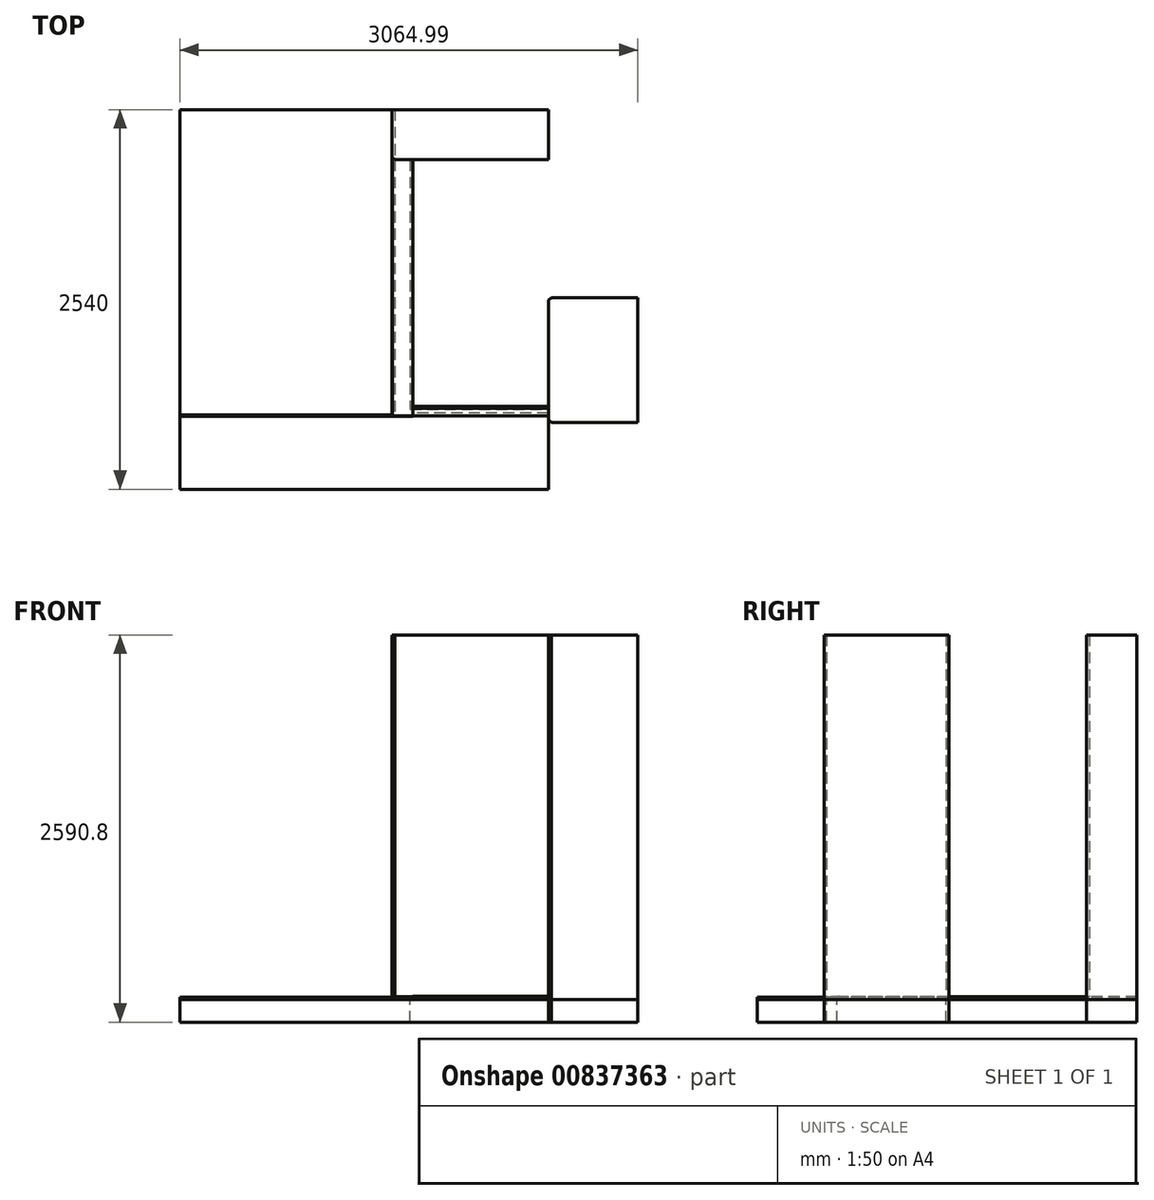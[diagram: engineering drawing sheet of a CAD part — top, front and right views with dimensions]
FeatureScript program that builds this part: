
annotation { "Feature Type Name" : "Feature", "Feature Type Description" : "" }
export const myFeature = defineFeature(function(context is Context, id is Id, definition is map)
    precondition{}
    {
        {
            var Q0;
            Q0=qCreatedBy(makeId("Top.planeOp"),FACE);
            var sketch = newSketch(context, id + "F0", { "sketchPlane" : qUnion([Q0])});
            skLineSegment(sketch, "E0.bottom", {"start": v(702.07, 1267.57) * mm, "end": v(-838.87, 1267.57) * mm});
            skLineSegment(sketch, "E0.top", {"start": v(702.07, -1272.43) * mm, "end": v(-838.87, -1272.43) * mm});
            skLineSegment(sketch, "E0.left", {"start": v(702.07, 1267.57) * mm, "end": v(702.07, -1272.43) * mm});
            skLineSegment(sketch, "E0.right", {"start": v(-838.87, 1267.57) * mm, "end": v(-838.87, -1272.43) * mm});
            skLineSegment(sketch, "E1.bottom", {"start": v(702.07, -1272.43) * mm, "end": v(1629.17, -1272.43) * mm});
            skLineSegment(sketch, "E1.top", {"start": v(702.07, -738.85) * mm, "end": v(1629.17, -738.85) * mm});
            skLineSegment(sketch, "E1.left", {"start": v(702.07, -1272.43) * mm, "end": v(702.07, -738.85) * mm});
            skLineSegment(sketch, "E1.right", {"start": v(1629.17, -1272.43) * mm, "end": v(1629.17, -738.85) * mm});
            skLineSegment(sketch, "E2.bottom", {"start": v(702.07, 1267.57) * mm, "end": v(1629.17, 1267.57) * mm});
            skLineSegment(sketch, "E2.top", {"start": v(702.07, 931.2) * mm, "end": v(1629.17, 931.2) * mm});
            skLineSegment(sketch, "E2.left", {"start": v(702.07, 1267.57) * mm, "end": v(702.07, 931.2) * mm});
            skLineSegment(sketch, "E2.right", {"start": v(1629.17, 1267.57) * mm, "end": v(1629.17, 931.2) * mm});
            skSolve(sketch);
        }
        {
            var Q0;
            Q0=makeQuery(id+"F0.imprint","IMPRINT",FACE,{"disambiguationData":[TD([[makeQuery(id+"F0.imprint","IMPRINT",EDGE,{"derivedFrom":sQuery(id+"F0.wireOp",EDGE,"E0.bottom")}),1.0]])]});
            var Q1;
            Q1=makeQuery(id+"F0.imprint","IMPRINT",FACE,{"disambiguationData":[TD([[makeQuery(id+"F0.imprint","IMPRINT",EDGE,{"derivedFrom":sQuery(id+"F0.wireOp",EDGE,"E2.bottom")}),-1.0]])]});
            var Q2;
            Q2=makeQuery(id+"F0.imprint","IMPRINT",FACE,{"disambiguationData":[TD([[makeQuery(id+"F0.imprint","IMPRINT",EDGE,{"derivedFrom":sQuery(id+"F0.wireOp",EDGE,"E1.bottom")}),1.0]])]});
            extrude(context, id + "F1", {"entities" : qUnion([Q0, Q1, Q2]), "oppositeDirection" : true, "depth" : 152.4 * mm, "offsetDistance" : 25.4 * mm});
        }
        {
            var Q0;
            Q0=makeQuery(id+"F1.opExtrude","CAP_FACE",FACE,{"disambiguationData":[OSD([sQuery(id+"F0.wireOp",EDGE,"E0.bottom"),sQuery(id+"F0.wireOp",EDGE,"E0.top"),sQuery(id+"F0.wireOp",EDGE,"E0.left"),sQuery(id+"F0.wireOp",EDGE,"E0.right"),sQuery(id+"F0.wireOp",EDGE,"E1.bottom"),sQuery(id+"F0.wireOp",EDGE,"E1.top"),sQuery(id+"F0.wireOp",EDGE,"E1.right"),sQuery(id+"F0.wireOp",EDGE,"E2.bottom"),sQuery(id+"F0.wireOp",EDGE,"E2.top"),sQuery(id+"F0.wireOp",EDGE,"E2.right")])],"isStart":true});
            var sketch = newSketch(context, id + "F2", { "sketchPlane" : qUnion([Q0])});
            skLineSegment(sketch, "E3", {"start": v(702.07, 931.2) * mm, "end": v(600.47, 931.2) * mm});
            skLineSegment(sketch, "E4", {"start": v(600.47, 931.2) * mm, "end": v(582.5, 949.16) * mm});
            skLineSegment(sketch, "E5", {"start": v(582.5, 949.16) * mm, "end": v(582.5, 1267.57) * mm});
            skLineSegment(sketch, "E6", {"start": v(582.5, 1267.57) * mm, "end": v(1629.17, 1267.57) * mm});
            skLineSegment(sketch, "E7", {"start": v(1629.17, 1267.57) * mm, "end": v(1629.17, 931.2) * mm});
            skLineSegment(sketch, "E8", {"start": v(1629.17, 931.2) * mm, "end": v(702.07, 931.2) * mm});
            skSolve(sketch);
        }
        {
            var Q0;
            Q0=makeQuery(id+"F2.imprint","IMPRINT",FACE,{"disambiguationData":[TD([[makeQuery(id+"F2.imprint","IMPRINT",EDGE,{"derivedFrom":sQuery(id+"F2.wireOp",EDGE,"E3")}),-1.0]])]});
            extrude(context, id + "F3", {"entities" : qUnion([Q0]), "depth" : 2438.4 * mm, "offsetDistance" : 25.4 * mm});
        }
        {
            var Q0;
            Q0=makeQuery(id+"F1.opExtrude","CAP_FACE",FACE,{"disambiguationData":[OSD([sQuery(id+"F0.wireOp",EDGE,"E0.bottom"),sQuery(id+"F0.wireOp",EDGE,"E0.top"),sQuery(id+"F0.wireOp",EDGE,"E0.left"),sQuery(id+"F0.wireOp",EDGE,"E0.right"),sQuery(id+"F0.wireOp",EDGE,"E1.bottom"),sQuery(id+"F0.wireOp",EDGE,"E1.top"),sQuery(id+"F0.wireOp",EDGE,"E1.right"),sQuery(id+"F0.wireOp",EDGE,"E2.bottom"),sQuery(id+"F0.wireOp",EDGE,"E2.top"),sQuery(id+"F0.wireOp",EDGE,"E2.right")])],"isStart":true});
            var sketch = newSketch(context, id + "F4", { "sketchPlane" : qUnion([Q0])});
            skLineSegment(sketch, "E9", {"start": v(1629.17, -808.7) * mm, "end": v(1629.17, -738.85) * mm});
            skLineSegment(sketch, "E10", {"start": v(1629.17, -738.85) * mm, "end": v(1629.17, -8.6) * mm});
            skLineSegment(sketch, "E11", {"start": v(1629.17, -8.6) * mm, "end": v(1647.13, 9.36) * mm});
            skLineSegment(sketch, "E12", {"start": v(1647.13, 9.36) * mm, "end": v(2226.12, 9.36) * mm});
            skLineSegment(sketch, "E13", {"start": v(1629.17, -808.7) * mm, "end": v(1647.13, -826.66) * mm});
            skLineSegment(sketch, "E14", {"start": v(1647.13, -826.66) * mm, "end": v(2226.12, -826.66) * mm});
            skLineSegment(sketch, "E15", {"start": v(2226.12, -826.66) * mm, "end": v(2226.12, 9.36) * mm});
            skSolve(sketch);
        }
        {
            var Q0;
            Q0=makeQuery(id+"F4.imprint","IMPRINT",FACE,{"disambiguationData":[TD([[makeQuery(id+"F4.imprint","IMPRINT",EDGE,{"derivedFrom":sQuery(id+"F4.wireOp",EDGE,"E9")}),-1.0]])]});
            var Q1;
            Q1=makeQuery(id+"F1.opExtrude","CAP_FACE",FACE,{"disambiguationData":[OSD([sQuery(id+"F0.wireOp",EDGE,"E0.bottom"),sQuery(id+"F0.wireOp",EDGE,"E0.top"),sQuery(id+"F0.wireOp",EDGE,"E0.left"),sQuery(id+"F0.wireOp",EDGE,"E0.right"),sQuery(id+"F0.wireOp",EDGE,"E1.bottom"),sQuery(id+"F0.wireOp",EDGE,"E1.top"),sQuery(id+"F0.wireOp",EDGE,"E1.right"),sQuery(id+"F0.wireOp",EDGE,"E2.bottom"),sQuery(id+"F0.wireOp",EDGE,"E2.top"),sQuery(id+"F0.wireOp",EDGE,"E2.right")])],"isStart":false});
            extrude(context, id + "F5", {"entities" : qUnion([Q0]), "operationType" : NewBodyOperationType.ADD, "endBound" : BoundingType.UP_TO_SURFACE, "oppositeDirection" : true, "depth" : 25.4 * mm, "endBoundEntityFace" : qUnion([Q1]), "offsetDistance" : 25.4 * mm});
        }
        {
            var Q0;
            Q0=makeQuery(id+"F4.imprint","IMPRINT",FACE,{"disambiguationData":[TD([[makeQuery(id+"F4.imprint","IMPRINT",EDGE,{"derivedFrom":sQuery(id+"F4.wireOp",EDGE,"E9")}),-1.0]])]});
            var Q1;
            Q1=makeQuery(id+"F3.opExtrude","CAP_FACE",FACE,{"disambiguationData":[OSD([sQuery(id+"F2.wireOp",EDGE,"E3"),sQuery(id+"F2.wireOp",EDGE,"E4"),sQuery(id+"F2.wireOp",EDGE,"E5"),sQuery(id+"F2.wireOp",EDGE,"E6"),sQuery(id+"F2.wireOp",EDGE,"E7"),sQuery(id+"F2.wireOp",EDGE,"E8")])],"isStart":false});
            extrude(context, id + "F6", {"entities" : qUnion([Q0]), "endBound" : BoundingType.UP_TO_SURFACE, "depth" : 25.4 * mm, "endBoundEntityFace" : qUnion([Q1]), "offsetDistance" : 25.4 * mm});
        }
        {
            var Q0;
            Q0=makeQuery(id+"F5.boolean.opBoolean","MERGE",FACE,{"derivedFrom":[makeQuery(id+"F1.opExtrude","CAP_FACE",FACE,{"disambiguationData":[OSD([sQuery(id+"F0.wireOp",EDGE,"E0.bottom"),sQuery(id+"F0.wireOp",EDGE,"E0.top"),sQuery(id+"F0.wireOp",EDGE,"E0.left"),sQuery(id+"F0.wireOp",EDGE,"E0.right"),sQuery(id+"F0.wireOp",EDGE,"E1.bottom"),sQuery(id+"F0.wireOp",EDGE,"E1.top"),sQuery(id+"F0.wireOp",EDGE,"E1.right"),sQuery(id+"F0.wireOp",EDGE,"E2.bottom"),sQuery(id+"F0.wireOp",EDGE,"E2.top"),sQuery(id+"F0.wireOp",EDGE,"E2.right")])],"isStart":true}),makeQuery(id+"F5.opExtrude","CAP_FACE",FACE,{"disambiguationData":[OSD([sQuery(id+"F4.wireOp",EDGE,"E9"),sQuery(id+"F4.wireOp",EDGE,"E10"),sQuery(id+"F4.wireOp",EDGE,"E11"),sQuery(id+"F4.wireOp",EDGE,"E12"),sQuery(id+"F4.wireOp",EDGE,"E13"),sQuery(id+"F4.wireOp",EDGE,"E14"),sQuery(id+"F4.wireOp",EDGE,"E15")])],"isStart":true})]});
            var sketch = newSketch(context, id + "F7", { "sketchPlane" : qUnion([Q0])});
            skLineSegment(sketch, "E16", {"start": v(600.47, 931.2) * mm, "end": v(582.5, 949.16) * mm});
            skLineSegment(sketch, "E17", {"start": v(582.5, 949.16) * mm, "end": v(582.5, -785.23) * mm});
            skLineSegment(sketch, "E18", {"start": v(721.12, 931.2) * mm, "end": v(721.12, -785.23) * mm});
            skLineSegment(sketch, "E19", {"start": v(721.12, -785.23) * mm, "end": v(582.5, -785.23) * mm});
            skLineSegment(sketch, "E20", {"start": v(600.47, 931.2) * mm, "end": v(721.12, 931.2) * mm});
            skSolve(sketch);
        }
        {
            var Q0;
            {var subQ4=sQuery(id+"F7.wireOp",EDGE,"E16");Q0=makeQuery(id+"F7.imprint","IMPRINT",FACE,{"disambiguationData":[TD([[makeQuery(id+"F7.imprint","IMPRINT",EDGE,{"derivedFrom":subQ4}),1.0]])]});}
            var Q1;
            {var subQ5=makeQuery(id+"F1.opExtrude","CAP_EDGE",EDGE,{"disambiguationData":[OSD([sQuery(id+"F0.wireOp",EDGE,"E0.left")])],"isStart":true});Q1=makeQuery(id+"F7.imprint","IMPRINT",FACE,{"disambiguationData":[TD([[makeQuery(id+"F7.imprint","IMPRINT",EDGE,{"derivedFrom":subQ5}),1.0]])]});}
            extrude(context, id + "F8", {"entities" : qUnion([Q0, Q1]), "depth" : 19.05 * mm, "offsetDistance" : 25.4 * mm});
        }
        {
            var Q0;
            Q0=makeQuery(id+"F5.boolean.opBoolean","MERGE",FACE,{"derivedFrom":[makeQuery(id+"F1.opExtrude","CAP_FACE",FACE,{"disambiguationData":[OSD([sQuery(id+"F0.wireOp",EDGE,"E0.bottom"),sQuery(id+"F0.wireOp",EDGE,"E0.top"),sQuery(id+"F0.wireOp",EDGE,"E0.left"),sQuery(id+"F0.wireOp",EDGE,"E0.right"),sQuery(id+"F0.wireOp",EDGE,"E1.bottom"),sQuery(id+"F0.wireOp",EDGE,"E1.top"),sQuery(id+"F0.wireOp",EDGE,"E1.right"),sQuery(id+"F0.wireOp",EDGE,"E2.bottom"),sQuery(id+"F0.wireOp",EDGE,"E2.top"),sQuery(id+"F0.wireOp",EDGE,"E2.right")])],"isStart":true}),makeQuery(id+"F5.opExtrude","CAP_FACE",FACE,{"disambiguationData":[OSD([sQuery(id+"F4.wireOp",EDGE,"E9"),sQuery(id+"F4.wireOp",EDGE,"E10"),sQuery(id+"F4.wireOp",EDGE,"E11"),sQuery(id+"F4.wireOp",EDGE,"E12"),sQuery(id+"F4.wireOp",EDGE,"E13"),sQuery(id+"F4.wireOp",EDGE,"E14"),sQuery(id+"F4.wireOp",EDGE,"E15")])],"isStart":true})]});
            var sketch = newSketch(context, id + "F9", { "sketchPlane" : qUnion([Q0])});
            skLineSegment(sketch, "E21", {"start": v(582.5, 1267.57) * mm, "end": v(-838.87, 1267.57) * mm});
            skLineSegment(sketch, "E22", {"start": v(-838.87, 1267.57) * mm, "end": v(-838.87, -1272.43) * mm});
            skLineSegment(sketch, "E23", {"start": v(-838.87, -1272.43) * mm, "end": v(1629.17, -1272.43) * mm});
            skLineSegment(sketch, "E24", {"start": v(1629.17, -1272.43) * mm, "end": v(1629.17, -779.67) * mm});
            skLineSegment(sketch, "E25", {"start": v(1629.17, -779.67) * mm, "end": v(597.3, -779.67) * mm});
            skLineSegment(sketch, "E26", {"start": v(582.5, 1267.57) * mm, "end": v(582.5, 949.16) * mm});
            skLineSegment(sketch, "E27", {"start": v(582.5, 949.16) * mm, "end": v(597.3, 934.37) * mm});
            skLineSegment(sketch, "E28", {"start": v(597.3, 934.37) * mm, "end": v(597.3, -779.67) * mm});
            skSolve(sketch);
        }
        {
            var Q0;
            Q0=makeQuery(id+"F9.imprint","IMPRINT",FACE,{"disambiguationData":[TD([[makeQuery(id+"F9.imprint","IMPRINT",EDGE,{"derivedFrom":sQuery(id+"F9.wireOp",EDGE,"E21")}),1.0]])]});
            extrude(context, id + "F10", {"entities" : qUnion([Q0]), "depth" : 2.3 * mm, "offsetDistance" : 25.4 * mm});
        }
        {
            var Q0;
            Q0=makeQuery(id+"F10.opExtrude","CAP_FACE",FACE,{"disambiguationData":[OSD([sQuery(id+"F9.wireOp",EDGE,"E21"),sQuery(id+"F9.wireOp",EDGE,"E22"),sQuery(id+"F9.wireOp",EDGE,"E23"),sQuery(id+"F9.wireOp",EDGE,"E24"),sQuery(id+"F9.wireOp",EDGE,"E25"),sQuery(id+"F9.wireOp",EDGE,"E26"),sQuery(id+"F9.wireOp",EDGE,"E27"),sQuery(id+"F9.wireOp",EDGE,"E28")])],"isStart":false});
            extrude(context, id + "F11", {"entities" : qUnion([Q0]), "depth" : 11.43 * mm, "offsetDistance" : 25.4 * mm});
        }
        {
            var Q0;
            Q0=makeQuery(id+"F8.opExtrude","SWEPT_FACE",FACE,{"disambiguationData":[OSD([sQuery(id+"F7.wireOp",EDGE,"E18")])]});
            var sketch = newSketch(context, id + "F12", { "sketchPlane" : qUnion([Q0])});
            skLineSegment(sketch, "E29", {"start": v(-738.85, 0) * mm, "end": v(-762.98, 0) * mm});
            skLineSegment(sketch, "E30", {"start": v(-762.98, 0) * mm, "end": v(-762.98, 14.48) * mm});
            skLineSegment(sketch, "E31", {"start": v(-762.98, 14.48) * mm, "end": v(-778.22, 14.48) * mm});
            skLineSegment(sketch, "E32", {"start": v(-778.22, 19.56) * mm, "end": v(-729.7, 19.56) * mm});
            skLineSegment(sketch, "E33", {"start": v(-738.85, 0) * mm, "end": v(-738.85, -3.3) * mm});
            skLineSegment(sketch, "E34", {"start": v(-738.85, -3.3) * mm, "end": v(-729.7, -3.3) * mm});
            skArc(sketch, "E35", {"start": v(-729.7, -3.3) * mm, "mid": v(-717.9, 8.13) * mm, "end": v(-729.7, 19.56) * mm});
            skLineSegment(sketch, "E36", {"start": v(-717.9, 8.13) * mm, "end": v(-778.22, 8.13) * mm, "construction": true});
            skPoint(sketch, "E36.startSnap0", {"position": v(-717.9, 8.13) * mm});
            skArc(sketch, "E37", {"start": v(-778.22, 19.56) * mm, "mid": v(-780.76, 17.02) * mm, "end": v(-778.22, 14.48) * mm});
            skSolve(sketch);
        }
        {
            var Q0;
            {var subQ9=sQuery(id+"F12.wireOp",EDGE,"E29");Q0=makeQuery(id+"F12.imprint","IMPRINT",FACE,{"disambiguationData":[TD([[makeQuery(id+"F12.imprint","IMPRINT",EDGE,{"derivedFrom":subQ9}),-1.0]])]});}
            var Q1;
            {var subQ0=sQuery(id+"F12.wireOp",EDGE,"E32");Q1=makeQuery(id+"F12.imprint","IMPRINT",FACE,{"disambiguationData":[TD([[makeQuery(id+"F12.imprint","IMPRINT",EDGE,{"derivedFrom":subQ0}),-1.0]])]});}
            var Q2;
            Q2=makeQuery(id+"F1.opExtrude","SWEPT_FACE",FACE,{"disambiguationData":[OSD([sQuery(id+"F0.wireOp",EDGE,"E1.right")])]});
            extrude(context, id + "F13", {"entities" : qUnion([Q0, Q1]), "endBound" : BoundingType.UP_TO_SURFACE, "depth" : 25.4 * mm, "endBoundEntityFace" : qUnion([Q2]), "offsetDistance" : 25.4 * mm});
        }
        {
            var Q0;
            Q0=makeQuery(id+"F8.opExtrude","SWEPT_FACE",FACE,{"disambiguationData":[OSD([sQuery(id+"F7.wireOp",EDGE,"E19")])]});
            var sketch = newSketch(context, id + "F14", { "sketchPlane" : qUnion([Q0])});
            skLineSegment(sketch, "E38", {"start": v(585.68, 19.05) * mm, "end": v(582.5, 15.88) * mm});
            skLineSegment(sketch, "E39", {"start": v(582.5, 15.88) * mm, "end": v(582.5, 19.05) * mm});
            skLineSegment(sketch, "E40", {"start": v(582.5, 19.05) * mm, "end": v(585.68, 19.05) * mm});
            skSolve(sketch);
        }
        {
            var Q0;
            Q0=makeQuery(id+"F14.imprint","IMPRINT",FACE,{"disambiguationData":[TD([[makeQuery(id+"F14.imprint","IMPRINT",EDGE,{"derivedFrom":sQuery(id+"F14.wireOp",EDGE,"E38")}),-1.0]])]});
            extrude(context, id + "F15", {"entities" : qUnion([Q0]), "operationType" : NewBodyOperationType.REMOVE, "endBound" : BoundingType.THROUGH_ALL, "oppositeDirection" : true, "depth" : 25.4 * mm, "offsetDistance" : 25.4 * mm});
        }
        {
            var Q0;
            Q0=makeQuery(id+"F8.opExtrude","SWEPT_FACE",FACE,{"disambiguationData":[OSD([sQuery(id+"F7.wireOp",EDGE,"E19")])]});
            var sketch = newSketch(context, id + "F16", { "sketchPlane" : qUnion([Q0])});
            skLineSegment(sketch, "E41", {"start": v(582.5, 13.72) * mm, "end": v(600.47, 13.72) * mm});
            skLineSegment(sketch, "E42", {"start": v(600.47, 13.72) * mm, "end": v(600.47, 0) * mm});
            skLineSegment(sketch, "E43", {"start": v(600.47, 0) * mm, "end": v(582.5, 0) * mm});
            skLineSegment(sketch, "E44", {"start": v(582.5, 0) * mm, "end": v(582.5, 13.72) * mm});
            skSolve(sketch);
        }
        {
            var Q0;
            Q0 = qSketchRegion(id + "F16", true);
            var Q1;
            Q1=makeQuery(id+"F16.imprint","IMPRINT",FACE,{"disambiguationData":[TD([[makeQuery(id+"F16.imprint","IMPRINT",EDGE,{"derivedFrom":sQuery(id+"F16.wireOp",EDGE,"E41")}),-1.0]])]});
            extrude(context, id + "F17", {"entities" : qUnion([Q0, Q1]), "operationType" : NewBodyOperationType.REMOVE, "endBound" : BoundingType.THROUGH_ALL, "oppositeDirection" : true, "depth" : 25.4 * mm, "offsetDistance" : 25.4 * mm});
        }
        {
            var Q0;
            Q0=makeQuery(id+"F8.opExtrude","SWEPT_FACE",FACE,{"disambiguationData":[OSD([sQuery(id+"F7.wireOp",EDGE,"E18")])]});
            var sketch = newSketch(context, id + "F18", { "sketchPlane" : qUnion([Q0])});
            skLineSegment(sketch, "E45", {"start": v(-785.23, 19.05) * mm, "end": v(-782.06, 19.05) * mm});
            skLineSegment(sketch, "E46", {"start": v(-782.06, 19.05) * mm, "end": v(-785.23, 15.87) * mm});
            skLineSegment(sketch, "E47", {"start": v(-785.23, 15.88) * mm, "end": v(-785.23, 19.05) * mm});
            skSolve(sketch);
        }
        {
            var Q0;
            Q0=makeQuery(id+"F18.imprint","IMPRINT",FACE,{"disambiguationData":[TD([[makeQuery(id+"F18.imprint","IMPRINT",EDGE,{"derivedFrom":sQuery(id+"F18.wireOp",EDGE,"E45")}),1.0]])]});
            extrude(context, id + "F19", {"entities" : qUnion([Q0]), "operationType" : NewBodyOperationType.REMOVE, "endBound" : BoundingType.THROUGH_ALL, "oppositeDirection" : true, "depth" : 25.4 * mm, "offsetDistance" : 25.4 * mm});
        }
        {
            var Q0;
            Q0=makeQuery(id+"F8.opExtrude","SWEPT_FACE",FACE,{"disambiguationData":[OSD([sQuery(id+"F7.wireOp",EDGE,"E18")])]});
            var sketch = newSketch(context, id + "F20", { "sketchPlane" : qUnion([Q0])});
            skLineSegment(sketch, "E48", {"start": v(-785.23, 13.72) * mm, "end": v(-776.5, 13.72) * mm});
            skLineSegment(sketch, "E49", {"start": v(-776.5, 13.72) * mm, "end": v(-776.5, 0) * mm});
            skLineSegment(sketch, "E50", {"start": v(-776.5, 0) * mm, "end": v(-785.23, 0) * mm});
            skLineSegment(sketch, "E51", {"start": v(-785.23, 0) * mm, "end": v(-785.23, 13.72) * mm});
            skSolve(sketch);
        }
        {
            var Q0;
            Q0=makeQuery(id+"F20.imprint","IMPRINT",FACE,{"disambiguationData":[TD([[makeQuery(id+"F20.imprint","IMPRINT",EDGE,{"derivedFrom":sQuery(id+"F20.wireOp",EDGE,"E48")}),-1.0]])]});
            extrude(context, id + "F21", {"entities" : qUnion([Q0]), "operationType" : NewBodyOperationType.REMOVE, "endBound" : BoundingType.THROUGH_ALL, "oppositeDirection" : true, "depth" : 25.4 * mm, "offsetDistance" : 25.4 * mm});
        }
    });
